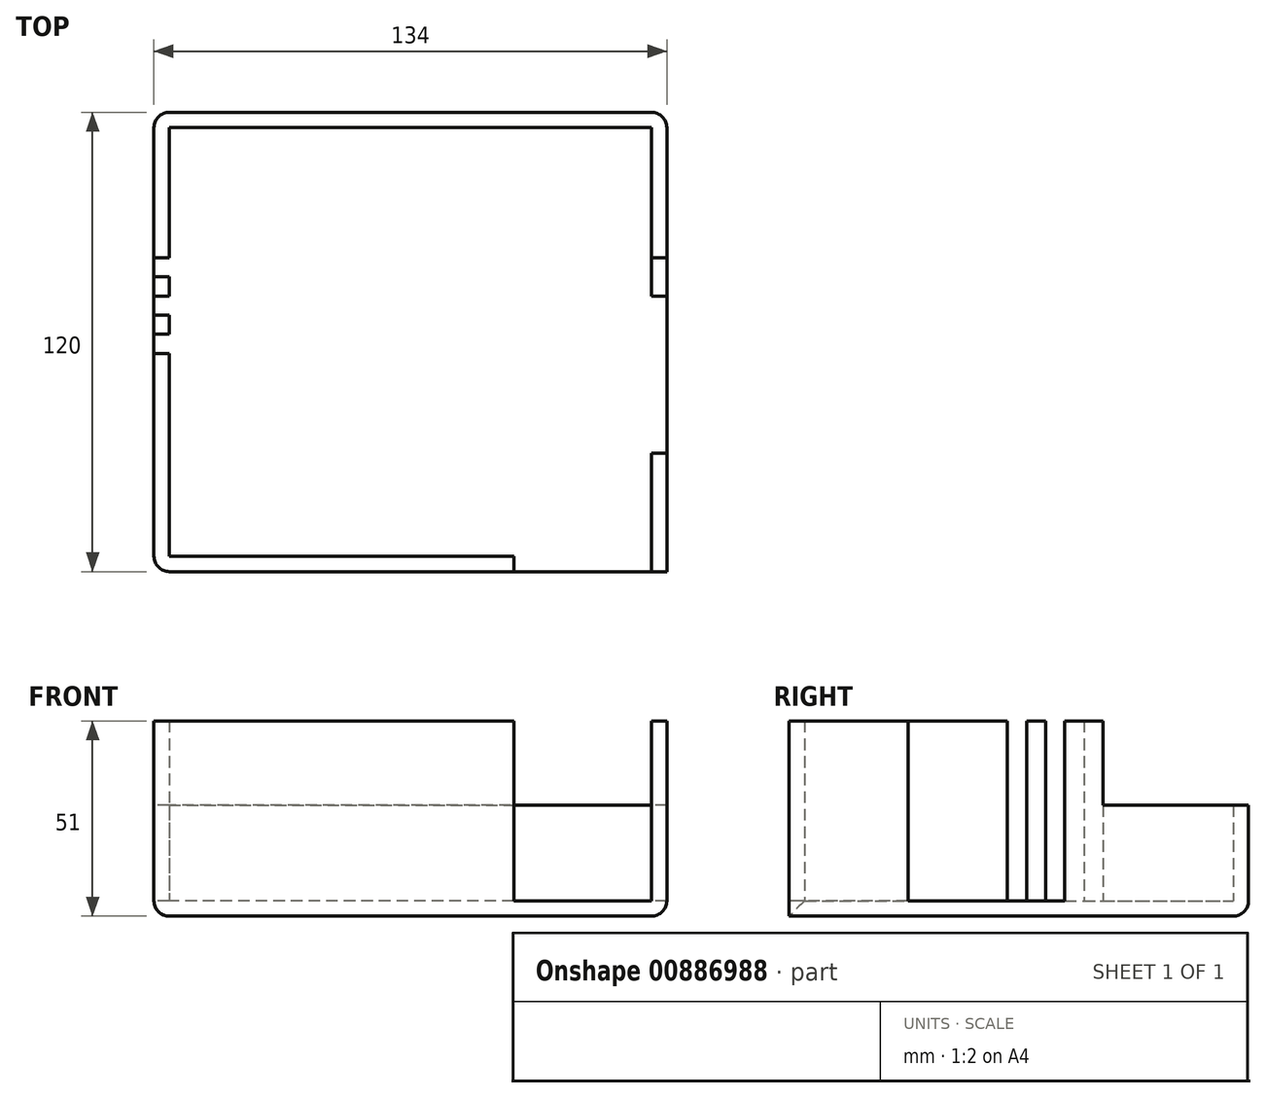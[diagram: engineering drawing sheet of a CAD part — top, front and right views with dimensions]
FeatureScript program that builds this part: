
annotation { "Feature Type Name" : "Feature", "Feature Type Description" : "" }
export const myFeature = defineFeature(function(context is Context, id is Id, definition is map)
    precondition{}
    {
        {
            var Q0;
            Q0=qCreatedBy(makeId("Top.planeOp"),FACE);
            var sketch = newSketch(context, id + "F0", { "sketchPlane" : qUnion([Q0])});
            skLineSegment(sketch, "E0.top", {"start": v(0, 0) * mm, "end": v(40, 0) * mm});
            skLineSegment(sketch, "E1.bottom", {"start": v(40, 0) * mm, "end": v(-94, 0) * mm});
            skLineSegment(sketch, "E1.top", {"start": v(40, 120) * mm, "end": v(-94, 120) * mm});
            skLineSegment(sketch, "E1.left", {"start": v(40, 0) * mm, "end": v(40, 120) * mm});
            skLineSegment(sketch, "E1.right", {"start": v(-94, 0) * mm, "end": v(-94, 120) * mm});
            skLineSegment(sketch, "E2.bottom", {"start": v(-70, 116) * mm, "end": v(36, 116) * mm, "construction": true});
            skLineSegment(sketch, "E2.top", {"start": v(-70, 13) * mm, "end": v(36, 13) * mm, "construction": true});
            skLineSegment(sketch, "E2.left", {"start": v(-70, 116) * mm, "end": v(-70, 13) * mm, "construction": true});
            skLineSegment(sketch, "E2.right", {"start": v(36, 116) * mm, "end": v(36, 13) * mm, "construction": true});
            skLineSegment(sketch, "E3.bottom", {"start": v(-90, 116) * mm, "end": v(36, 116) * mm});
            skLineSegment(sketch, "E3.top", {"start": v(-90, 4) * mm, "end": v(36, 4) * mm});
            skLineSegment(sketch, "E3.left", {"start": v(-90, 116) * mm, "end": v(-90, 4) * mm});
            skLineSegment(sketch, "E3.right", {"start": v(36, 116) * mm, "end": v(36, 4) * mm});
            skLineSegment(sketch, "E4", {"start": v(0, 0) * mm, "end": v(0, 4) * mm});
            skLineSegment(sketch, "E5", {"start": v(36, 4) * mm, "end": v(36, 0) * mm});
            skLineSegment(sketch, "E6", {"start": v(40, 72) * mm, "end": v(36, 72) * mm});
            skLineSegment(sketch, "E7", {"start": v(40, 31) * mm, "end": v(36, 31) * mm});
            skLineSegment(sketch, "E8", {"start": v(40, 82) * mm, "end": v(-94, 82) * mm});
            skLineSegment(sketch, "E9", {"start": v(-94, 72) * mm, "end": v(-74.46, 72) * mm, "construction": true});
            skLineSegment(sketch, "E10", {"start": v(-94, 77) * mm, "end": v(-90, 77) * mm});
            skLineSegment(sketch, "E11", {"start": v(-94, 72) * mm, "end": v(-90, 72) * mm});
            skLineSegment(sketch, "E12", {"start": v(-94, 67) * mm, "end": v(-90, 67) * mm});
            skPoint(sketch, "E12.endSnap0", {"position": v(-90, 60) * mm});
            skLineSegment(sketch, "E13", {"start": v(-94, 62) * mm, "end": v(-90, 62) * mm});
            skLineSegment(sketch, "E14", {"start": v(-94, 57) * mm, "end": v(-90, 57) * mm});
            skSolve(sketch);
        }
        {
            var Q0;
            {var subQ1=sQuery(id+"F0.wireOp",EDGE,"E1.top");Q0=makeQuery(id+"F0.imprint","IMPRINT",FACE,{"disambiguationData":[TD([[makeQuery(id+"F0.imprint","IMPRINT",EDGE,{"derivedFrom":subQ1}),1.0]])]});}
            var Q1;
            {var subQ6=sQuery(id+"F0.wireOp",EDGE,"E1.bottom");Q1=makeQuery(id+"F0.imprint","IMPRINT",FACE,{"disambiguationData":[TD([[makeQuery(id+"F0.imprint","IMPRINT",EDGE,{"derivedFrom":subQ6}),-1.0]])]});}
            var Q2;
            {var subQ2=sQuery(id+"F0.wireOp",EDGE,"E6");Q2=makeQuery(id+"F0.imprint","IMPRINT",FACE,{"disambiguationData":[TD([[makeQuery(id+"F0.imprint","IMPRINT",EDGE,{"derivedFrom":subQ2}),1.0]])]});}
            var Q3;
            {var subQ3=sQuery(id+"F0.wireOp",EDGE,"E6");Q3=makeQuery(id+"F0.imprint","IMPRINT",FACE,{"disambiguationData":[TD([[makeQuery(id+"F0.imprint","IMPRINT",EDGE,{"derivedFrom":subQ3}),-1.0]])]});}
            var Q4;
            {var subQ3=sQuery(id+"F0.wireOp",EDGE,"E10");Q4=makeQuery(id+"F0.imprint","IMPRINT",FACE,{"disambiguationData":[TD([[makeQuery(id+"F0.imprint","IMPRINT",EDGE,{"derivedFrom":subQ3}),1.0]])]});}
            var Q5;
            {var subQ0=sQuery(id+"F0.wireOp",EDGE,"E13");Q5=makeQuery(id+"F0.imprint","IMPRINT",FACE,{"disambiguationData":[TD([[makeQuery(id+"F0.imprint","IMPRINT",EDGE,{"derivedFrom":subQ0}),-1.0]])]});}
            var Q6;
            Q6 = qSketchRegion(id + "FE51uc5lEMIJbnQ_1", true);
            var Q7;
            {var subQ0=sQuery(id+"F0.wireOp",EDGE,"E11");Q7=makeQuery(id+"F0.imprint","IMPRINT",FACE,{"disambiguationData":[TD([[makeQuery(id+"F0.imprint","IMPRINT",EDGE,{"derivedFrom":subQ0}),-1.0]])]});}
            var Q8;
            {var subQ0=sQuery(id+"F0.wireOp",EDGE,"E10");Q8=makeQuery(id+"F0.imprint","IMPRINT",FACE,{"disambiguationData":[TD([[makeQuery(id+"F0.imprint","IMPRINT",EDGE,{"derivedFrom":subQ0}),-1.0]])]});}
            var Q9;
            {var subQ0=sQuery(id+"F0.wireOp",EDGE,"E12");Q9=makeQuery(id+"F0.imprint","IMPRINT",FACE,{"disambiguationData":[TD([[makeQuery(id+"F0.imprint","IMPRINT",EDGE,{"derivedFrom":subQ0}),-1.0]])]});}
            var Q10;
            {var subQ0=sQuery(id+"F0.wireOp",EDGE,"E13");Q10=makeQuery(id+"F0.imprint","IMPRINT",FACE,{"disambiguationData":[TD([[makeQuery(id+"F0.imprint","IMPRINT",EDGE,{"derivedFrom":subQ0}),-1.0]])]});}
            var Q11;
            {var subQ3=sQuery(id+"F0.wireOp",EDGE,"E10");Q11=makeQuery(id+"F0.imprint","IMPRINT",FACE,{"disambiguationData":[TD([[makeQuery(id+"F0.imprint","IMPRINT",EDGE,{"derivedFrom":subQ3}),1.0]])]});}
            var Q12;
            Q12=makeQuery(id+"F0.imprint","IMPRINT",FACE,{"disambiguationData":[TD([[makeQuery(id+"F0.imprint","IMPRINT",EDGE,{"derivedFrom":sQuery(id+"F0.wireOp",EDGE,"3S3MyepO-jsnd-322W-3zAR-mHp1B6YM8ZqH")}),-1.0]])]});
            var Q13;
            {var subQ0=sQuery(id+"F0.wireOp",EDGE,"E4");Q13=makeQuery(id+"F0.imprint","IMPRINT",FACE,{"disambiguationData":[TD([[makeQuery(id+"F0.imprint","IMPRINT",EDGE,{"derivedFrom":subQ0}),-1.0]])]});}
            var Q14;
            {var subQ0=sQuery(id+"F0.wireOp",EDGE,"E3.bottom");Q14=makeQuery(id+"F0.imprint","IMPRINT",FACE,{"disambiguationData":[TD([[makeQuery(id+"F0.imprint","IMPRINT",EDGE,{"derivedFrom":subQ0}),-1.0]])]});}
            var Q15;
            {var subQ3=sQuery(id+"F0.wireOp",EDGE,"E3.left");var subQ11=sQuery(id+"F0.wireOp",EDGE,"E3.top");var subQ13=makeQuery(id+"F0.imprint","INTERSECT",VERTEX,{"derivedFrom":[subQ11,subQ3]});Q15=makeQuery(id+"F0.imprint","IMPRINT",FACE,{"disambiguationData":[TD([[makeQuery(id+"F0.imprint","IMPRINT",EDGE,{"disambiguationData":[TD([[subQ13,-1.0]])],"derivedFrom":subQ11}),1.0]])]});}
            var Q16;
            {var subQ0=sQuery(id+"F0.wireOp",EDGE,"E11");Q16=makeQuery(id+"F0.imprint","IMPRINT",FACE,{"disambiguationData":[TD([[makeQuery(id+"F0.imprint","IMPRINT",EDGE,{"derivedFrom":subQ0}),-1.0]])]});}
            extrude(context, id + "F1", {"entities" : qUnion([Q0, Q1, Q2, Q3, Q4, Q5, Q6, Q7, Q8, Q9, Q10, Q11, Q12, Q13, Q14, Q15, Q16]), "depth" : 4 * mm, "offsetDistance" : 25 * mm});
        }
        {
            var Q0;
            {var subQ0=sQuery(id+"F0.wireOp",EDGE,"E5");Q0=makeQuery(id+"F0.imprint","IMPRINT",FACE,{"disambiguationData":[TD([[makeQuery(id+"F0.imprint","IMPRINT",EDGE,{"derivedFrom":subQ0}),1.0]])]});}
            var Q1;
            {var subQ3=sQuery(id+"F0.wireOp",EDGE,"E6");Q1=makeQuery(id+"F0.imprint","IMPRINT",FACE,{"disambiguationData":[TD([[makeQuery(id+"F0.imprint","IMPRINT",EDGE,{"derivedFrom":subQ3}),-1.0]])]});}
            var Q2;
            {var subQ6=sQuery(id+"F0.wireOp",EDGE,"E1.bottom");Q2=makeQuery(id+"F0.imprint","IMPRINT",FACE,{"disambiguationData":[TD([[makeQuery(id+"F0.imprint","IMPRINT",EDGE,{"derivedFrom":subQ6}),-1.0]])]});}
            extrude(context, id + "F2", {"entities" : qUnion([Q0, Q1, Q2]), "operationType" : NewBodyOperationType.ADD, "depth" : 51 * mm, "offsetDistance" : 25 * mm});
        }
        {
            var Q0;
            {var subQ1=sQuery(id+"F0.wireOp",EDGE,"E1.top");Q0=makeQuery(id+"F0.imprint","IMPRINT",FACE,{"disambiguationData":[TD([[makeQuery(id+"F0.imprint","IMPRINT",EDGE,{"derivedFrom":subQ1}),1.0]])]});}
            extrude(context, id + "F3", {"entities" : qUnion([Q0]), "operationType" : NewBodyOperationType.ADD, "depth" : 29 * mm, "offsetDistance" : 25 * mm});
        }
        {
            var Q0;
            {var subQ0=sQuery(id+"F0.wireOp",EDGE,"E1.left");Q0=makeQuery(id+"F2.boolean.opBoolean","MERGE",EDGE,{"derivedFrom":[makeQuery(id+"F1.opExtrude","CAP_EDGE",EDGE,{"disambiguationData":[OSD([subQ0])],"isStart":true}),makeQuery(id+"F2.opExtrude","CAP_EDGE",EDGE,{"disambiguationData":[OSD([subQ0]),TDD([makeQuery(id+"F0.imprint","IMPRINT",EDGE,{"disambiguationData":[TD([[makeQuery(id+"F0.imprint","INTERSECT",VERTEX,{"derivedFrom":[sQuery(id+"F0.wireOp",EDGE,"E0.top"),subQ0]}),-1.0]])],"derivedFrom":subQ0})])],"isStart":true})]});}
            var Q1;
            Q1=makeQuery(id+"F1.opExtrude","CAP_EDGE",EDGE,{"disambiguationData":[OSD([sQuery(id+"F0.wireOp",EDGE,"E1.top")])],"isStart":true});
            var Q2;
            {var subQ0=sQuery(id+"F0.wireOp",EDGE,"E1.left");var subQ1=sQuery(id+"F0.wireOp",EDGE,"E1.top");Q2=makeQuery(id+"F3.boolean.opBoolean","MERGE",EDGE,{"derivedFrom":[makeQuery(id+"F1.opExtrude","SWEPT_EDGE",EDGE,{"disambiguationData":[OSD([subQ1,subQ0])]}),makeQuery(id+"F3.opExtrude","SWEPT_EDGE",EDGE,{"disambiguationData":[OSD([subQ1,subQ0])]})]});}
            var Q3;
            {var subQ0=sQuery(id+"F0.wireOp",EDGE,"E1.left");var subQ1=sQuery(id+"F0.wireOp",EDGE,"E1.top");Q3=makeQuery(id+"F3.boolean.opBoolean","MERGE",EDGE,{"derivedFrom":[makeQuery(id+"F1.opExtrude","SWEPT_EDGE",EDGE,{"disambiguationData":[OSD([subQ1,subQ0])]}),makeQuery(id+"F3.opExtrude","SWEPT_EDGE",EDGE,{"disambiguationData":[OSD([subQ1,subQ0])]})]});}
            var Q4;
            Q4=makeQuery(id+"F1.opExtrude","CAP_EDGE",EDGE,{"disambiguationData":[OSD([sQuery(id+"F0.wireOp",EDGE,"E1.top")])],"isStart":true});
            var Q5;
            {var subQ0=sQuery(id+"F0.wireOp",EDGE,"E1.right");var subQ1=sQuery(id+"F0.wireOp",EDGE,"E1.top");Q5=makeQuery(id+"F3.boolean.opBoolean","MERGE",EDGE,{"derivedFrom":[makeQuery(id+"F1.opExtrude","SWEPT_EDGE",EDGE,{"disambiguationData":[OSD([subQ1,subQ0])]}),makeQuery(id+"F3.opExtrude","SWEPT_EDGE",EDGE,{"disambiguationData":[OSD([subQ1,subQ0])]})]});}
            var Q6;
            Q6=makeQuery(id+"F1.opExtrude","CAP_EDGE",EDGE,{"disambiguationData":[OSD([sQuery(id+"F0.wireOp",EDGE,"E1.right")])],"isStart":true});
            var Q7;
            {var subQ0=sQuery(id+"F0.wireOp",EDGE,"E1.right");var subQ1=sQuery(id+"F0.wireOp",EDGE,"E1.bottom");Q7=makeQuery(id+"F2.boolean.opBoolean","MERGE",EDGE,{"derivedFrom":[makeQuery(id+"F1.opExtrude","SWEPT_EDGE",EDGE,{"disambiguationData":[OSD([subQ1,subQ0])]}),makeQuery(id+"F2.opExtrude","SWEPT_EDGE",EDGE,{"disambiguationData":[OSD([subQ1,subQ0])]})]});}
            var Q8;
            {var subQ0=sQuery(id+"F0.wireOp",EDGE,"E1.bottom");Q8=makeQuery(id+"F2.opExtrude","CAP_EDGE",EDGE,{"disambiguationData":[OSD([subQ0]),TDD([makeQuery(id+"F0.imprint","IMPRINT",EDGE,{"disambiguationData":[TD([[makeQuery(id+"F0.imprint","INTERSECT",VERTEX,{"derivedFrom":[subQ0,sQuery(id+"F0.wireOp",EDGE,"E1.right")]}),1.0]])],"derivedFrom":subQ0})])],"isStart":true});}
            var Q9;
            {var subQ0=sQuery(id+"F0.wireOp",EDGE,"E1.left");Q9=makeQuery(id+"F2.boolean.opBoolean","MERGE",EDGE,{"derivedFrom":[makeQuery(id+"F1.opExtrude","CAP_EDGE",EDGE,{"disambiguationData":[OSD([subQ0])],"isStart":true}),makeQuery(id+"F2.opExtrude","CAP_EDGE",EDGE,{"disambiguationData":[OSD([subQ0]),TDD([makeQuery(id+"F0.imprint","IMPRINT",EDGE,{"disambiguationData":[TD([[makeQuery(id+"F0.imprint","INTERSECT",VERTEX,{"derivedFrom":[sQuery(id+"F0.wireOp",EDGE,"E0.top"),subQ0]}),-1.0]])],"derivedFrom":subQ0})])],"isStart":true})]});}
            var Q10;
            {var subQ0=sQuery(id+"F0.wireOp",EDGE,"E1.bottom");Q10=makeQuery(id+"F2.opExtrude","CAP_EDGE",EDGE,{"disambiguationData":[OSD([subQ0]),TDD([makeQuery(id+"F0.imprint","IMPRINT",EDGE,{"disambiguationData":[TD([[makeQuery(id+"F0.imprint","INTERSECT",VERTEX,{"derivedFrom":[subQ0,sQuery(id+"F0.wireOp",EDGE,"E1.right")]}),1.0]])],"derivedFrom":subQ0})])],"isStart":true});}
            var Q11;
            Q11=makeQuery(id+"F2.opExtrude","CAP_EDGE",EDGE,{"disambiguationData":[OSD([sQuery(id+"F0.wireOp",EDGE,"E1.right")])],"isStart":true});
            var Q12;
            {var subQ0=sQuery(id+"F0.wireOp",EDGE,"E1.right");var subQ1=sQuery(id+"F0.wireOp",EDGE,"E1.bottom");Q12=makeQuery(id+"F2.boolean.opBoolean","MERGE",EDGE,{"derivedFrom":[makeQuery(id+"F1.opExtrude","SWEPT_EDGE",EDGE,{"disambiguationData":[OSD([subQ1,subQ0])]}),makeQuery(id+"F2.opExtrude","SWEPT_EDGE",EDGE,{"disambiguationData":[OSD([subQ1,subQ0])]})]});}
            var Q13;
            {var subQ0=sQuery(id+"F0.wireOp",EDGE,"E1.left");Q13=makeQuery(id+"F2.boolean.opBoolean","MERGE",EDGE,{"derivedFrom":[makeQuery(id+"F1.opExtrude","CAP_EDGE",EDGE,{"disambiguationData":[OSD([subQ0])],"isStart":true}),makeQuery(id+"F2.opExtrude","CAP_EDGE",EDGE,{"disambiguationData":[OSD([subQ0]),TDD([makeQuery(id+"F0.imprint","IMPRINT",EDGE,{"disambiguationData":[TD([[makeQuery(id+"F0.imprint","INTERSECT",VERTEX,{"derivedFrom":[sQuery(id+"F0.wireOp",EDGE,"E0.top"),subQ0]}),-1.0]])],"derivedFrom":subQ0})])],"isStart":true})]});}
            var Q14;
            {var subQ0=sQuery(id+"F0.wireOp",EDGE,"E1.left");var subQ1=sQuery(id+"F0.wireOp",EDGE,"E1.top");Q14=makeQuery(id+"F3.boolean.opBoolean","MERGE",EDGE,{"derivedFrom":[makeQuery(id+"F1.opExtrude","SWEPT_EDGE",EDGE,{"disambiguationData":[OSD([subQ1,subQ0])]}),makeQuery(id+"F3.opExtrude","SWEPT_EDGE",EDGE,{"disambiguationData":[OSD([subQ1,subQ0])]})]});}
            var Q15;
            {var subQ0=sQuery(id+"F0.wireOp",EDGE,"E1.left");Q15=makeQuery(id+"F2.opExtrude","CAP_EDGE",EDGE,{"disambiguationData":[OSD([subQ0]),TDD([makeQuery(id+"F0.imprint","IMPRINT",EDGE,{"disambiguationData":[TD([[makeQuery(id+"F0.imprint","INTERSECT",VERTEX,{"derivedFrom":[subQ0,sQuery(id+"F0.wireOp",EDGE,"E6")]}),-1.0]])],"derivedFrom":subQ0})])],"isStart":true});}
            var Q16;
            {var subQ0=sQuery(id+"F0.wireOp",EDGE,"E1.left");Q16=makeQuery(id+"F2.boolean.opBoolean","MERGE",EDGE,{"derivedFrom":[makeQuery(id+"F1.opExtrude","CAP_EDGE",EDGE,{"disambiguationData":[OSD([subQ0])],"isStart":true}),makeQuery(id+"F2.opExtrude","CAP_EDGE",EDGE,{"disambiguationData":[OSD([subQ0]),TDD([makeQuery(id+"F0.imprint","IMPRINT",EDGE,{"disambiguationData":[TD([[makeQuery(id+"F0.imprint","INTERSECT",VERTEX,{"derivedFrom":[sQuery(id+"F0.wireOp",EDGE,"E0.top"),subQ0]}),-1.0]])],"derivedFrom":subQ0})])],"isStart":true})]});}
            var Q17;
            {var subQ0=sQuery(id+"F0.wireOp",EDGE,"E1.left");var subQ1=sQuery(id+"F0.wireOp",EDGE,"E1.top");Q17=makeQuery(id+"F3.boolean.opBoolean","MERGE",EDGE,{"derivedFrom":[makeQuery(id+"F1.opExtrude","SWEPT_EDGE",EDGE,{"disambiguationData":[OSD([subQ1,subQ0])]}),makeQuery(id+"F3.opExtrude","SWEPT_EDGE",EDGE,{"disambiguationData":[OSD([subQ1,subQ0])]})]});}
            var Q18;
            {var subQ0=sQuery(id+"F0.wireOp",EDGE,"E1.right");var subQ1=sQuery(id+"F0.wireOp",EDGE,"E1.top");Q18=makeQuery(id+"F3.boolean.opBoolean","MERGE",EDGE,{"derivedFrom":[makeQuery(id+"F1.opExtrude","SWEPT_EDGE",EDGE,{"disambiguationData":[OSD([subQ1,subQ0])]}),makeQuery(id+"F3.opExtrude","SWEPT_EDGE",EDGE,{"disambiguationData":[OSD([subQ1,subQ0])]})]});}
            var Q19;
            {var subQ0=sQuery(id+"F0.wireOp",EDGE,"E1.right");var subQ1=sQuery(id+"F0.wireOp",EDGE,"E1.bottom");Q19=makeQuery(id+"F2.boolean.opBoolean","MERGE",EDGE,{"derivedFrom":[makeQuery(id+"F1.opExtrude","SWEPT_EDGE",EDGE,{"disambiguationData":[OSD([subQ1,subQ0])]}),makeQuery(id+"F2.opExtrude","SWEPT_EDGE",EDGE,{"disambiguationData":[OSD([subQ1,subQ0])]})]});}
            var Q20;
            Q20=makeQuery(id+"F1.opExtrude","CAP_EDGE",EDGE,{"disambiguationData":[OSD([sQuery(id+"F0.wireOp",EDGE,"E1.right")])],"isStart":true});
            var Q21;
            Q21=makeQuery(id+"F3.opExtrude","CAP_EDGE",EDGE,{"disambiguationData":[OSD([sQuery(id+"F0.wireOp",EDGE,"E1.right")])],"isStart":true});
            var Q22;
            Q22=makeQuery(id+"F1.opExtrude","CAP_EDGE",EDGE,{"disambiguationData":[OSD([sQuery(id+"F0.wireOp",EDGE,"E1.right")])],"isStart":true});
            var Q23;
            Q23=makeQuery(id+"F1.opExtrude","CAP_EDGE",EDGE,{"disambiguationData":[OSD([sQuery(id+"F0.wireOp",EDGE,"E1.top")])],"isStart":true});
            var Q24;
            Q24=makeQuery(id+"F1.opExtrude","CAP_EDGE",EDGE,{"disambiguationData":[OSD([sQuery(id+"F0.wireOp",EDGE,"E1.top")])],"isStart":true});
            fillet(context, id + "F4", {"entities" : qUnion([Q0, Q1, Q2, Q3, Q4, Q5, Q6, Q7, Q8, Q9, Q10, Q11, Q12, Q13, Q14, Q15, Q16, Q17, Q18, Q19, Q20, Q21, Q22, Q23, Q24]), "radius" : 4 * mm, "tangentPropagation" : true, "allowEdgeOverflow" : false});
        }
        {
            var Q0;
            {var subQ0=sQuery(id+"F0.wireOp",EDGE,"E10");Q0=makeQuery(id+"F0.imprint","IMPRINT",FACE,{"disambiguationData":[TD([[makeQuery(id+"F0.imprint","IMPRINT",EDGE,{"derivedFrom":subQ0}),-1.0]])]});}
            var Q1;
            {var subQ0=sQuery(id+"F0.wireOp",EDGE,"E12");Q1=makeQuery(id+"F0.imprint","IMPRINT",FACE,{"disambiguationData":[TD([[makeQuery(id+"F0.imprint","IMPRINT",EDGE,{"derivedFrom":subQ0}),-1.0]])]});}
            extrude(context, id + "F5", {"entities" : qUnion([Q0, Q1]), "operationType" : NewBodyOperationType.ADD, "depth" : 51 * mm, "offsetDistance" : 25 * mm});
        }
        {
            var Q0;
            {var subQ0=sQuery(id+"F0.wireOp",EDGE,"E1.right");Q0=makeQuery(id+"F5.opExtrude","CAP_EDGE",EDGE,{"disambiguationData":[OSD([subQ0]),TDD([makeQuery(id+"F0.imprint","IMPRINT",EDGE,{"disambiguationData":[TD([[makeQuery(id+"F0.imprint","INTERSECT",VERTEX,{"derivedFrom":[subQ0,sQuery(id+"F0.wireOp",EDGE,"E10")]}),1.0]])],"derivedFrom":subQ0})])],"isStart":true});}
            var Q1;
            {var subQ0=sQuery(id+"F0.wireOp",EDGE,"E1.right");Q1=makeQuery(id+"F5.opExtrude","CAP_EDGE",EDGE,{"disambiguationData":[OSD([subQ0]),TDD([makeQuery(id+"F0.imprint","IMPRINT",EDGE,{"disambiguationData":[TD([[makeQuery(id+"F0.imprint","INTERSECT",VERTEX,{"derivedFrom":[subQ0,sQuery(id+"F0.wireOp",EDGE,"E12")]}),1.0]])],"derivedFrom":subQ0})])],"isStart":true});}
            var Q2;
            Q2=makeQuery(id+"F3.opExtrude","CAP_EDGE",EDGE,{"disambiguationData":[OSD([sQuery(id+"F0.wireOp",EDGE,"E1.top")])],"isStart":true});
            fillet(context, id + "F6", {"entities" : qUnion([Q0, Q1, Q2]), "radius" : 4 * mm, "tangentPropagation" : true, "allowEdgeOverflow" : false});
        }
    });
